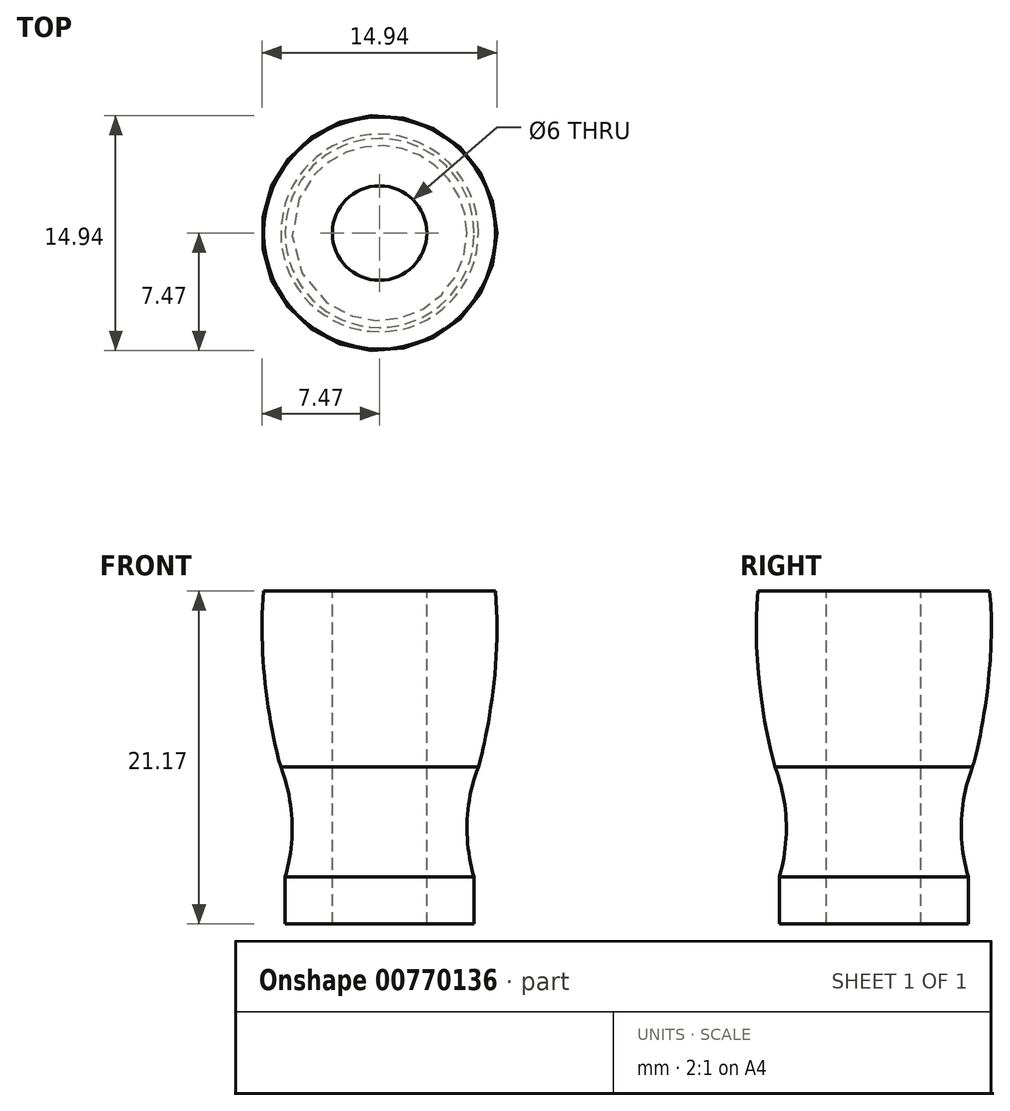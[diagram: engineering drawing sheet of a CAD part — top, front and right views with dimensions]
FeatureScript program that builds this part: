
annotation { "Feature Type Name" : "Feature", "Feature Type Description" : "" }
export const myFeature = defineFeature(function(context is Context, id is Id, definition is map)
    precondition{}
    {
        {
            var Q0;
            Q0=qCreatedBy(makeId("Right.planeOp"),FACE);
            var sketch = newSketch(context, id + "F0", { "sketchPlane" : qUnion([Q0])});
            skLineSegment(sketch, "E0", {"start": v(6, 0) * mm, "end": v(6, 3) * mm});
            skArc(sketch, "E1", {"start": v(6.27, 9.97) * mm, "mid": v(5.56, 6.5) * mm, "end": v(6, 3) * mm});
            skLineSegment(sketch, "E2", {"start": v(0, 26.9) * mm, "end": v(0, -5.2) * mm, "construction": true});
            skLineSegment(sketch, "E3", {"start": v(3, 0) * mm, "end": v(3, 21.17) * mm});
            skLineSegment(sketch, "E4", {"start": v(3, 21.17) * mm, "end": v(7.36, 21.17) * mm});
            skLineSegment(sketch, "E5", {"start": v(3, 0) * mm, "end": v(6, 0) * mm});
            skFitSpline(sketch, "E6", {"points": [v(6.27, 9.97) * mm, v(7, 13.36) * mm, v(7.36, 21.17) * mm], "startDerivative": vector(1.6, 5.3) * mm, "endDerivative": vector(-1.3, 13.84) * mm});
            skSolve(sketch);
        }
        {
            var Q0;
            Q0=makeQuery(id+"F0.imprint","IMPRINT",FACE,{"disambiguationData":[TD([[makeQuery(id+"F0.imprint","IMPRINT",EDGE,{"derivedFrom":sQuery(id+"F0.wireOp",EDGE,"E0")}),1.0]])]});
            var Q1;
            Q1=sQuery(id+"F0.wireOp",EDGE,"E2");
            revolve(context, id + "F1", {"surfaceOperationType" : NewSurfaceOperationType.NEW, "entities" : qUnion([Q0]), "axis" : qUnion([Q1]), "revolveType" : RevolveType.FULL});
        }
    });
